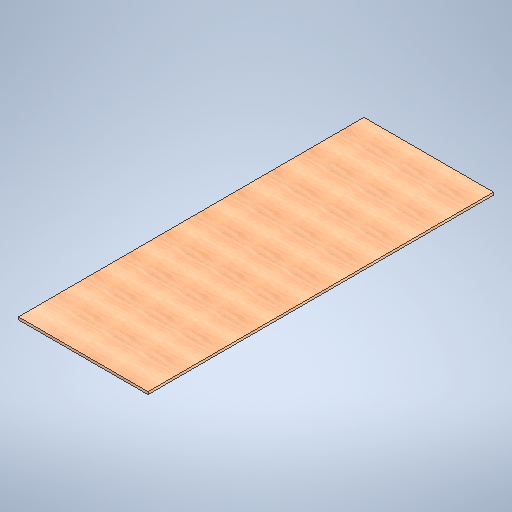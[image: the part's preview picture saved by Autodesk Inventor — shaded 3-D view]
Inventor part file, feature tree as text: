
AUTODESK INVENTOR PART (.ipt)
format: ipt  version: 2025 (Build 290162010, 162A)  size: 318,976 bytes
history: native  units: in
note: dims shown in document units (in); Inventor stores cm internally (conversion verified against a paired STEP export)
features: extrude x1, sketch x1
ambient origin geometry x8: Origin, YZ Plane, XZ Plane, XY Plane, X Axis, Y Axis, Z Axis, Center Point
bodies: Solid1 (feature_tree)
feature tree (2):
  extrude  "Extrusion1"  Depth=36.0in
  sketch  "Sketch1"  dims[d2=96.0in d3=36.0in d4=0.7188in d5=0.0in]
